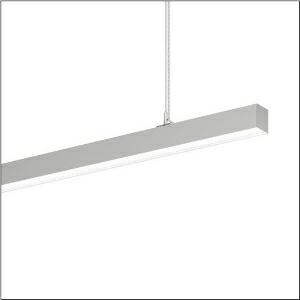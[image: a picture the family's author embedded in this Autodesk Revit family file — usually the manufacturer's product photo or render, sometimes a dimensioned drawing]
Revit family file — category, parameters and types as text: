
# Revit family: silica_21_51mx33da47sb
name_source: partatom
category: Lighting Fixtures
units: mm (PartAtom-declared; Revit-internal decimal feet)

## family parameters
Cut with Voids When Loaded = No
Host = Face
Light Source = No
Part Type = Normal
Room Calculation Point = No
Round Connector Dimension = Use Diameter
Shared = No

## types (1)
- --- (1 x LED, 5910 lm, 38.4 W, 4000K)
    Apparent Load = 38 VA
    CIE Flux Codes = 78 96 99 55 100
    Color Rendering = 80
    Color Temperature = 4000K
    Default Elevation = 1800 mm
    Description = Silica 21, office luminaire, primary optical cover: prismatic diffuser, of PMMA, CAT 2 (L<= 3000cd/m²), light emission: direct/indirect distribution, primary light characteristic: symmetric, installation type: suspended mounting, LED, rated luminous flux: 5.910lm, luminous efficacy: 154lm/W, light colour: 840, colour temperature: 4000K, control gear: DALI 2, with terminal, 3+2-pole, max. 2.5mm², mains connection: 220..240V, AC, 50/60Hz, rated input power: 38.4W, luminaire housing, of aluminium, metallic grey (RAL 9006), length: 1.204mm, width: 53mm, height: 53mm, protection rating (complete): IP20, insulation class (complete): insulation class I (protective earthing), certification: CE, permissible operating ambient temperature: 0..+35°C, standard: EN 50419, packaging unit: 1 piece
    Height = 53 mm
    Lamp = 1 x LED
    Lamp Light Flux = 5910 lm
    Lamp Power = 38.4 W
    Lamp count = 1
    Length = 1204 mm
    Luminous efficacy = 154 lm/W
    Manufacturer = Siteco
    ModVariant = No
    Model = 51MX33DA47SB
    Mounting Place = Ceiling
    Mounting Type = Pendant
    Number of Poles = 1
    OnlyDefault = Yes
    Power Factor = 1
    Product Name = Silica 21
    Product group = office luminaire | ceiling pendant
    ProductGroupID = 903
    Protection Class = Protection class I
    Protection Degree = IP 20
    RLX_Detail_Level = 1
    RLX_Emergency_Light_Flux = 0 lm
    RLX_Emergency_Type = 0
    RLX_Emergency_Type_DB = No
    RlxData = <blob elided: 23229 chars, md5=e48c56ec>
    Socket = socket
    Standby Power = 0 W
    System Light Flux = 5910 lm
    System Power = 38 W
    Type Comments = factory setting: luminous flux: 100 % | dim-lin: 254 | 322 mA
    Type Image = l_1335864.jpg
    URL = http://relux.com
    VarID = @adj_118755
    Voltage = 0 V
    Weight = 0.00 kg
    Width = 53 mm

## geometry (parser evidence)
native form markers: Blend x4, Sweep x11
no freeform markers — native parametric forms only
